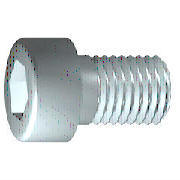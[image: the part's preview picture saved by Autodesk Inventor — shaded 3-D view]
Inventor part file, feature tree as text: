
AUTODESK INVENTOR PART (.ipt)
format: ipt  version: 2017 (Build 210142000, 142)  size: 181,760 bytes
history: native  units: mm (DEFAULTED — no unit token found)
features: sketch x2, extrude x1, plane x1, fillet x1
ambient origin geometry x7: Origin, YZ Plane, XY Plane, X Axis, Y Axis, Z Axis, Center Point
bodies: Solid1 (feature_tree), Body (feature_tree)
feature tree (5):
  extrude  "Slot"  Depth=3.0mm
  plane  "Work Plane1"
  fillet  "Fillet2"  Radius=3.0mm
  sketch  "Sketch1"  dims[d1=18.0mm d2=0.306825mm d3=3.0mm]
  sketch  "Sketch2"  dims[d4=1.5mm d5=60.0deg d6=3.0mm d7=3.0mm d8=2.886751mm d9=5.5mm d10=90.0deg d11=10.0mm d12=0.0mm d13=18.0mm d14=0.0mm d15=0.306725mm d16=0.306725mm d17=0.3mm d19=0.0mm d26=35.0mm d27=45.0deg d28=0.0mm d29=0.0mm d30=0.1mm]
